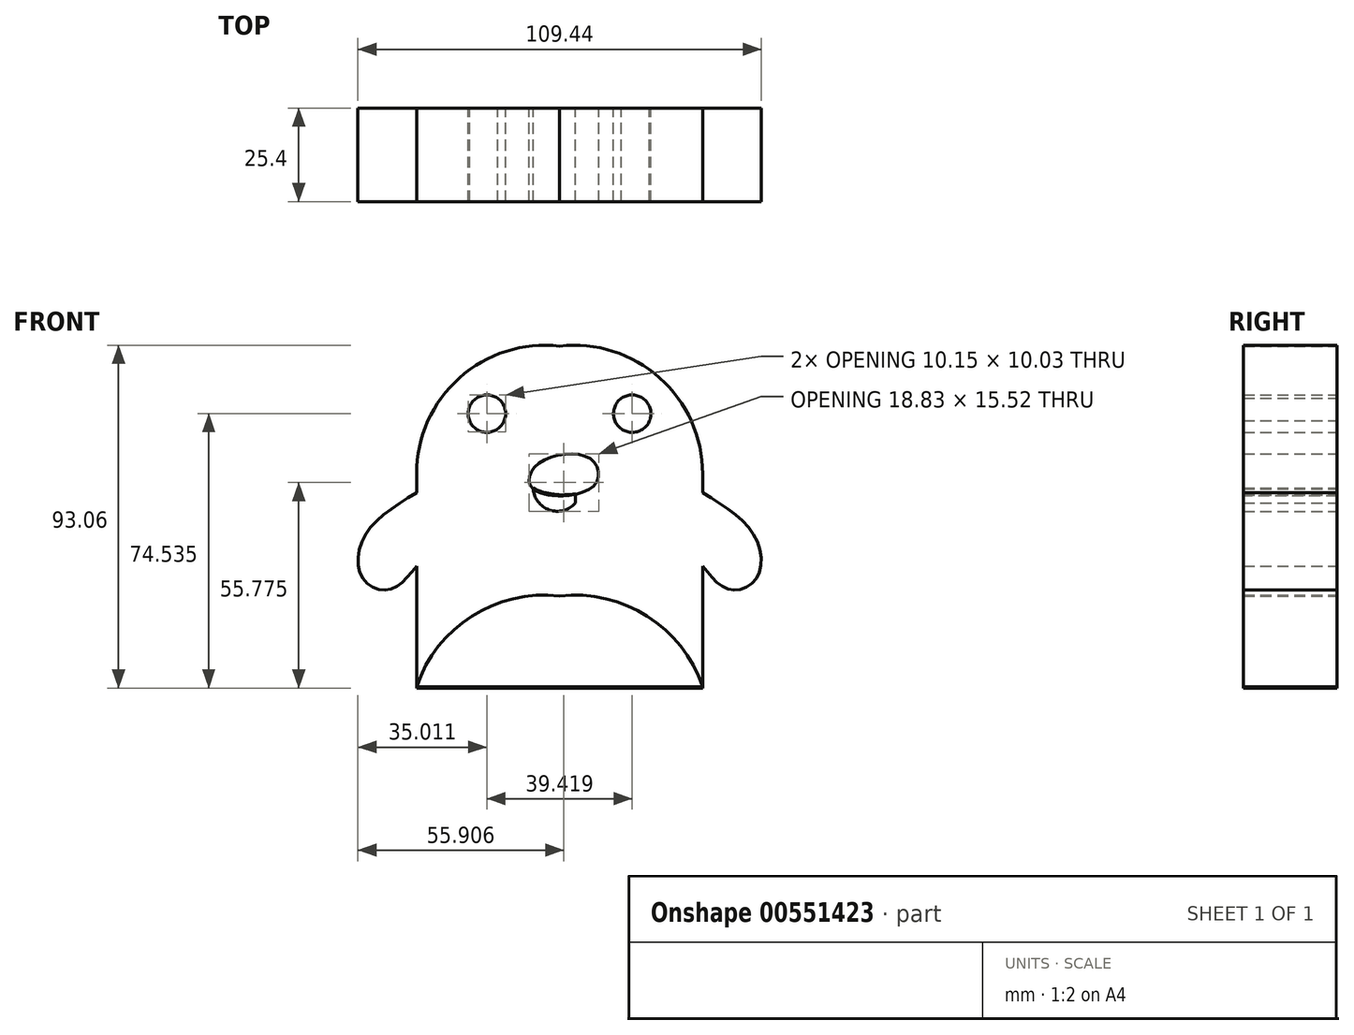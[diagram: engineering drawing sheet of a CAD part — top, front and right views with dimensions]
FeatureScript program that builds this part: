
annotation { "Feature Type Name" : "Feature", "Feature Type Description" : "" }
export const myFeature = defineFeature(function(context is Context, id is Id, definition is map)
    precondition{}
    {
        {
            var Q0;
            Q0=qCreatedBy(makeId("Front.planeOp"),FACE);
            var sketch = newSketch(context, id + "F0", { "sketchPlane" : qUnion([Q0])});
            skLineSegment(sketch, "E0", {"start": v(-38.81, -32.89) * mm, "end": v(0, -32.89) * mm});
            skLineSegment(sketch, "E1", {"start": v(-38.81, -32.89) * mm, "end": v(-38.81, 25.02) * mm});
            skArc(sketch, "E2", {"start": v(0, 59.68) * mm, "mid": v(-27.16, 51.04) * mm, "end": v(-38.81, 25.02) * mm});
            skLineSegment(sketch, "E3", {"start": v(0, 70) * mm, "end": v(0, -64.97) * mm, "construction": true});
            skArc(sketch, "E4", {"start": v(0, -8.18) * mm, "mid": v(-23.78, -13.66) * mm, "end": v(-38.81, -32.89) * mm});
            skArc(sketch, "E5.MirrorCS", {"start": v(0, 59.68) * mm, "mid": v(27.16, 51.04) * mm, "end": v(38.81, 25.02) * mm});
            skLineSegment(sketch, "E6.MirrorCS", {"start": v(38.81, -32.89) * mm, "end": v(38.81, 25.02) * mm});
            skArc(sketch, "E7.MirrorCS", {"start": v(0, -8.18) * mm, "mid": v(23.78, -13.66) * mm, "end": v(38.81, -32.89) * mm});
            skLineSegment(sketch, "E8.MirrorCS", {"start": v(38.81, -32.89) * mm, "end": v(0, -32.89) * mm});
            skFitSpline(sketch, "E9", {"points": [v(-5.97, 27.54) * mm, v(8.46, 29.05) * mm, v(9.06, 21.53) * mm, v(-7.17, 20.93) * mm, v(-5.97, 27.54) * mm]});
            skArc(sketch, "E10", {"start": v(-7.17, 20.93) * mm, "mid": v(-2.75, 15.2) * mm, "end": v(4.25, 17.02) * mm});
            skLineSegment(sketch, "E11", {"start": v(4.25, 17.02) * mm, "end": v(4.25, 19.42) * mm});
            skLineSegment(sketch, "E12", {"start": v(4.25, 19.42) * mm, "end": v(4.25, 17.02) * mm});
            skArc(sketch, "E13", {"start": v(-16.8, 45.5) * mm, "mid": v(-22.87, 45.27) * mm, "end": v(-24.43, 39.4) * mm});
            skArc(sketch, "E14", {"start": v(-24.43, 39.4) * mm, "mid": v(-16.54, 37.36) * mm, "end": v(-16.8, 45.5) * mm});
            skArc(sketch, "E15.MirrorCS", {"start": v(24.43, 39.4) * mm, "mid": v(16.54, 37.36) * mm, "end": v(16.8, 45.5) * mm});
            skArc(sketch, "E16.MirrorCS", {"start": v(16.8, 45.5) * mm, "mid": v(22.87, 45.27) * mm, "end": v(24.43, 39.4) * mm});
            skFitSpline(sketch, "E17", {"points": [v(-38.81, 19.85) * mm, v(-52.9, 8.1) * mm, v(-53.44, -3.36) * mm, v(-46.11, -6.41) * mm, v(-38.81, 0) * mm], "startDerivative": vector(-54.15, -32.88) * mm, "endDerivative": vector(29, 37.66) * mm});
            skFitSpline(sketch, "E18.MirrorCS", {"points": [v(38.81, 19.85) * mm, v(52.9, 8.1) * mm, v(53.44, -3.36) * mm, v(46.11, -6.41) * mm, v(38.81, 0) * mm], "startDerivative": vector(54.15, -32.88) * mm, "endDerivative": vector(-29, 37.66) * mm});
            skLineSegment(sketch, "E19", {"start": v(-7.17, 20.93) * mm, "end": v(-7.17, 21.14) * mm});
            skLineSegment(sketch, "E20", {"start": v(4.25, 19.42) * mm, "end": v(4.25, 19.63) * mm});
            skArc(sketch, "E21", {"start": v(-7.17, 21.14) * mm, "mid": v(-1.58, 19.45) * mm, "end": v(4.25, 19.63) * mm});
            skLineSegment(sketch, "E22", {"start": v(-38.81, -32.89) * mm, "end": v(-38.81, -33.16) * mm});
            skLineSegment(sketch, "E23", {"start": v(-38.81, -33.16) * mm, "end": v(38.82, -33.16) * mm});
            skLineSegment(sketch, "E24", {"start": v(38.82, -33.16) * mm, "end": v(38.81, -32.89) * mm});
            skSolve(sketch);
        }
        {
            var Q0;
            {var subQ0=sQuery(id+"F0.wireOp",EDGE,"E17");Q0=makeQuery(id+"F0.imprint","IMPRINT",FACE,{"disambiguationData":[TD([[makeQuery(id+"F0.imprint","IMPRINT",EDGE,{"derivedFrom":subQ0}),1.0]])]});}
            var Q1;
            {var subQ11=sQuery(id+"F0.wireOp",EDGE,"E2");Q1=makeQuery(id+"F0.imprint","IMPRINT",FACE,{"disambiguationData":[TD([[makeQuery(id+"F0.imprint","IMPRINT",EDGE,{"derivedFrom":subQ11}),1.0]])]});}
            var Q2;
            Q2=makeQuery(id+"F0.imprint","IMPRINT",FACE,{"disambiguationData":[TD([[makeQuery(id+"F0.imprint","IMPRINT",EDGE,{"derivedFrom":sQuery(id+"F0.wireOp",EDGE,"E0")}),-1.0]])]});
            var Q3;
            {var subQ0=sQuery(id+"F0.wireOp",EDGE,"E18.MirrorCS");Q3=makeQuery(id+"F0.imprint","IMPRINT",FACE,{"disambiguationData":[TD([[makeQuery(id+"F0.imprint","IMPRINT",EDGE,{"derivedFrom":subQ0}),-1.0]])]});}
            var Q4;
            {var subQ0=sQuery(id+"F0.wireOp",EDGE,"E19");Q4=makeQuery(id+"F0.imprint","IMPRINT",FACE,{"disambiguationData":[TD([[makeQuery(id+"F0.imprint","IMPRINT",EDGE,{"derivedFrom":subQ0}),-1.0]])]});}
            extrude(context, id + "F1", {"entities" : qUnion([Q0, Q1, Q2, Q3, Q4]), "depth" : 25.4 * mm, "offsetDistance" : 25.4 * mm});
        }
    });
